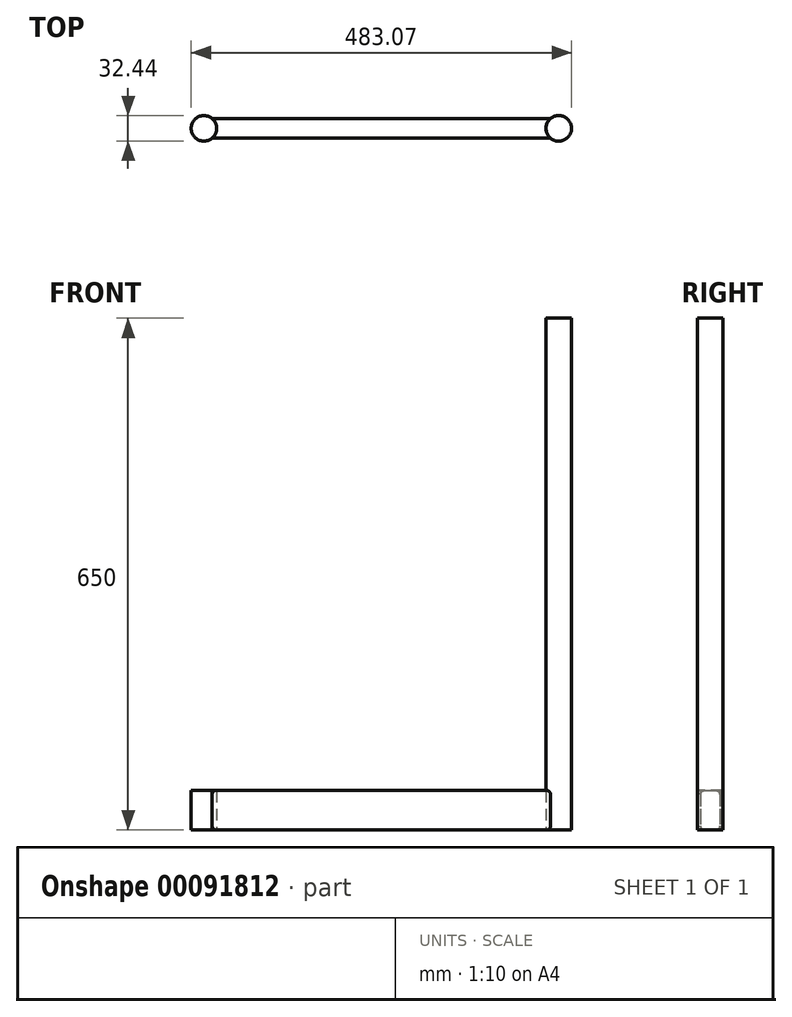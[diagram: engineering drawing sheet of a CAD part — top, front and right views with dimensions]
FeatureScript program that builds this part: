
annotation { "Feature Type Name" : "Feature", "Feature Type Description" : "" }
export const myFeature = defineFeature(function(context is Context, id is Id, definition is map)
    precondition{}
    {
        {
            var Q0;
            Q0=qCreatedBy(makeId("Top.planeOp"),FACE);
            var sketch = newSketch(context, id + "F0", { "sketchPlane" : qUnion([Q0])});
            skLineSegment(sketch, "E0.bottom", {"start": v(-131.2, -7.07) * mm, "end": v(298.8, -7.07) * mm});
            skLineSegment(sketch, "E0.top", {"start": v(-131.2, -32.07) * mm, "end": v(298.8, -32.07) * mm});
            skCircle(sketch, "E1", {"center": v(309.17, -19.57) * mm, "radius": 16.22 * mm});
            skPoint(sketch, "E1.centerSnap0", {"position": v(298.8, -19.57) * mm});
            skCircle(sketch, "E2", {"center": v(-141.48, -19.57) * mm, "radius": 16.22 * mm});
            skPoint(sketch, "E2.centerSnap0", {"position": v(-131.2, -19.57) * mm});
            skArc(sketch, "E3", {"start": v(-131.2, -32.07) * mm, "mid": v(-125.3, -19.57) * mm, "end": v(-131.2, -7.07) * mm});
            skArc(sketch, "E4", {"start": v(298.8, -7.07) * mm, "mid": v(292.98, -19.57) * mm, "end": v(298.8, -32.07) * mm});
            skSolve(sketch);
        }
        {
            var Q0;
            {var subQ0=sQuery(id+"F0.wireOp",EDGE,"E3");Q0=makeQuery(id+"F0.imprint","IMPRINT",FACE,{"disambiguationData":[TD([[makeQuery(id+"F0.imprint","IMPRINT",EDGE,{"derivedFrom":subQ0}),1.0]])]});}
            var Q1;
            {var subQ1=sQuery(id+"F0.wireOp",EDGE,"E0.bottom");var subQ5=sQuery(id+"F0.wireOp",EDGE,"E4");var subQ10=makeQuery(id+"F0.imprint","INTERSECT",VERTEX,{"derivedFrom":[subQ1,subQ5]});Q1=makeQuery(id+"F0.imprint","IMPRINT",FACE,{"disambiguationData":[TD([[makeQuery(id+"F0.imprint","IMPRINT",EDGE,{"disambiguationData":[TD([[subQ10,1.0]])],"derivedFrom":subQ1}),-1.0]])]});}
            extrude(context, id + "F1", {"entities" : qUnion([Q0, Q1]), "depth" : 50 * mm});
        }
        {
            var Q0;
            {var subQ0=sQuery(id+"F0.wireOp",EDGE,"E4");var subQ1=sQuery(id+"F0.wireOp",EDGE,"E1");var subQ2=makeQuery(id+"F0.imprint","INTERSECT",VERTEX,{"disambiguationData":[OD(0.0)],"derivedFrom":[subQ1,subQ0]});Q0=makeQuery(id+"F0.imprint","IMPRINT",FACE,{"disambiguationData":[TD([[makeQuery(id+"F0.imprint","IMPRINT",EDGE,{"disambiguationData":[TD([[subQ2,1.0]])],"derivedFrom":subQ1}),1.0]])]});}
            extrude(context, id + "F2", {"entities" : qUnion([Q0]), "depth" : 650 * mm});
        }
        {
            var Q0;
            {var subQ0=sQuery(id+"F0.wireOp",EDGE,"E0.top");Q0=makeQuery(id+"F1.opExtrude","CAP_EDGE",EDGE,{"disambiguationData":[OSD([subQ0]),TDD([makeQuery(id+"F0.imprint","IMPRINT",EDGE,{"disambiguationData":[TD([[makeQuery(id+"F0.imprint","INTERSECT",VERTEX,{"derivedFrom":[subQ0,sQuery(id+"F0.wireOp",EDGE,"E4")]}),1.0]])],"derivedFrom":subQ0})])],"isStart":false});}
            var Q1;
            {var subQ0=sQuery(id+"F0.wireOp",EDGE,"E0.bottom");Q1=makeQuery(id+"F1.opExtrude","CAP_EDGE",EDGE,{"disambiguationData":[OSD([subQ0]),TDD([makeQuery(id+"F0.imprint","IMPRINT",EDGE,{"disambiguationData":[TD([[makeQuery(id+"F0.imprint","INTERSECT",VERTEX,{"derivedFrom":[subQ0,sQuery(id+"F0.wireOp",EDGE,"E4")]}),1.0]])],"derivedFrom":subQ0})])],"isStart":false});}
            var Q2;
            {var subQ0=sQuery(id+"F0.wireOp",EDGE,"E0.top");Q2=makeQuery(id+"F1.opExtrude","CAP_EDGE",EDGE,{"disambiguationData":[OSD([subQ0]),TDD([makeQuery(id+"F0.imprint","IMPRINT",EDGE,{"disambiguationData":[TD([[makeQuery(id+"F0.imprint","INTERSECT",VERTEX,{"derivedFrom":[subQ0,sQuery(id+"F0.wireOp",EDGE,"E4")]}),1.0]])],"derivedFrom":subQ0})])],"isStart":true});}
            var Q3;
            {var subQ0=sQuery(id+"F0.wireOp",EDGE,"E0.bottom");Q3=makeQuery(id+"F1.opExtrude","CAP_EDGE",EDGE,{"disambiguationData":[OSD([subQ0]),TDD([makeQuery(id+"F0.imprint","IMPRINT",EDGE,{"disambiguationData":[TD([[makeQuery(id+"F0.imprint","INTERSECT",VERTEX,{"derivedFrom":[subQ0,sQuery(id+"F0.wireOp",EDGE,"E4")]}),1.0]])],"derivedFrom":subQ0})])],"isStart":true});}
            fillet(context, id + "F3", {"entities" : qUnion([Q0, Q1, Q2, Q3]), "radius" : 5.08 * mm, "tangentPropagation" : true, "allowEdgeOverflow" : false});
        }
    });
